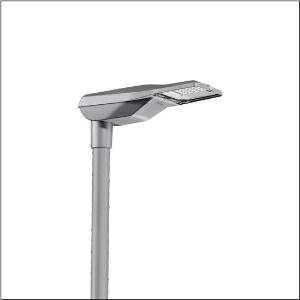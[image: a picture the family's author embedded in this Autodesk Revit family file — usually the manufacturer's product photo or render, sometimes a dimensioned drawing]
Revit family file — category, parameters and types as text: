
# Revit family: streetlight_sl_21_iq_micro___st1_0ab_5xe1m31g08cb_01f6
name_source: partatom
category: Lighting Fixtures
units: mm (PartAtom-declared; Revit-internal decimal feet)

## family parameters
Cut with Voids When Loaded = No
Host = Face
Light Source = No
Part Type = Normal
Room Calculation Point = No
Round Connector Dimension = Use Diameter
Shared = No

## types (1)
- --- (1 x LED, 2520 lm, 19.4 W, 3000K)
    Apparent Load = 19 VA
    CIE Flux Codes = 38 73 97 100 100
    Color Rendering = 70
    Color Temperature = 3000K
    Default Elevation = 1800 mm
    Description = Streetlight SL 21 iQ micro, mast luminaire, primary light control with lens, of PMMA, primary optical cover: cover, of toughened safety glass, transparent, light distribution: ST1.0aB, light emission: direct distribution, primary light characteristic: asymmetric, installation type: post-top, side-entry, LED, High Power LED, rated luminous flux: 2.520lm, luminous efficacy: 130lm/W, light colour: 730, colour temperature: 3000K, control: Street-Remote, Auto-Match, Temp-Guard, Lumen-Switch, Night-Set, Smart-Wire, Light-Fading, Desk-Remote (wireless, voltage-free reading and setting of iQ features in the workshop via application-optimized NFC function/RFID function), optimised constant luminous flux control (CLO 2.0), presetting dimming linear, mains connection: 220..240V, AC, 50/60Hz, start of lifetime: 19W, end of service life: 20W, reduction: 10W, luminaire housing, of diecast aluminium, powder-coated, Siteco® metallic grey (DB 702S), corrosivity category C5 mid according to DIN EN ISO 12944, please order mast flange separately, inclination adjustable: 0°, 5°, 10°, 15°, sealing non-destructively replaceable, multi-level sealing system, length: 528mm, width: 235mm, height: 110mm, mast flange for spigot size: 42mm (side-entry): 5XC10008XM4, 60/48mm (side-entry/post-top): 5XC10108XM2, 76/60mm (side-entry/post-top): 5XC10108XM1, protection rating (complete): IP66, insulation class (complete): insulation class II (safety insulation), certification: CE, ENEC, ENEC+, VDE, impact resistance: IK09, permissible operating ambient temperature for outdoor applications: -40..+50°C, standard-compliant lighting for roads and squares, packaging unit: 1 piece

Light Distribution: ST1.0aB
    Height = 110 mm
    Lamp = 1 x LED
    Lamp Light Flux = 2520 lm
    Lamp Power = 19.4 W
    Lamp count = 1
    Length = 528 mm
    Luminous efficacy = 130 lm/W
    Manufacturer = Siteco
    ModVariant = No
    Model = 5XE1M31G08CB
    Number of Poles = 1
    OnlyDefault = Yes
    Power Factor = 1
    Product Name = Streetlight SL 21 iQ micro | ST1.0aB
    Product group = mast luminaire | pylon top
    ProductGroupID = 6100
    Protection Class = Protection class II
    Protection Degree = IP 66
    RLX_Detail_Level = 1
    RLX_Emergency_Light_Flux = 0 lm
    RLX_Emergency_Type = 0
    RLX_Emergency_Type_DB = No
    RlxData = <blob elided: 98509 chars, md5=94ceaab0>
    Socket = socket
    Standby Power = 0 W
    System Light Flux = 2520 lm
    System Power = 19 W
    Type Comments = factory setting: luminous flux: 100 % | dim-lin: 254 | 387 mA
    Type Image = l_1006881.jpg
    URL = http://relux.com
    VarID = @adj_069469
    Voltage = 0 V
    Weight = 0.00 kg
    Width = 235 mm

## geometry (parser evidence)
native form markers: Blend x4, Sweep x10
no freeform markers — native parametric forms only
